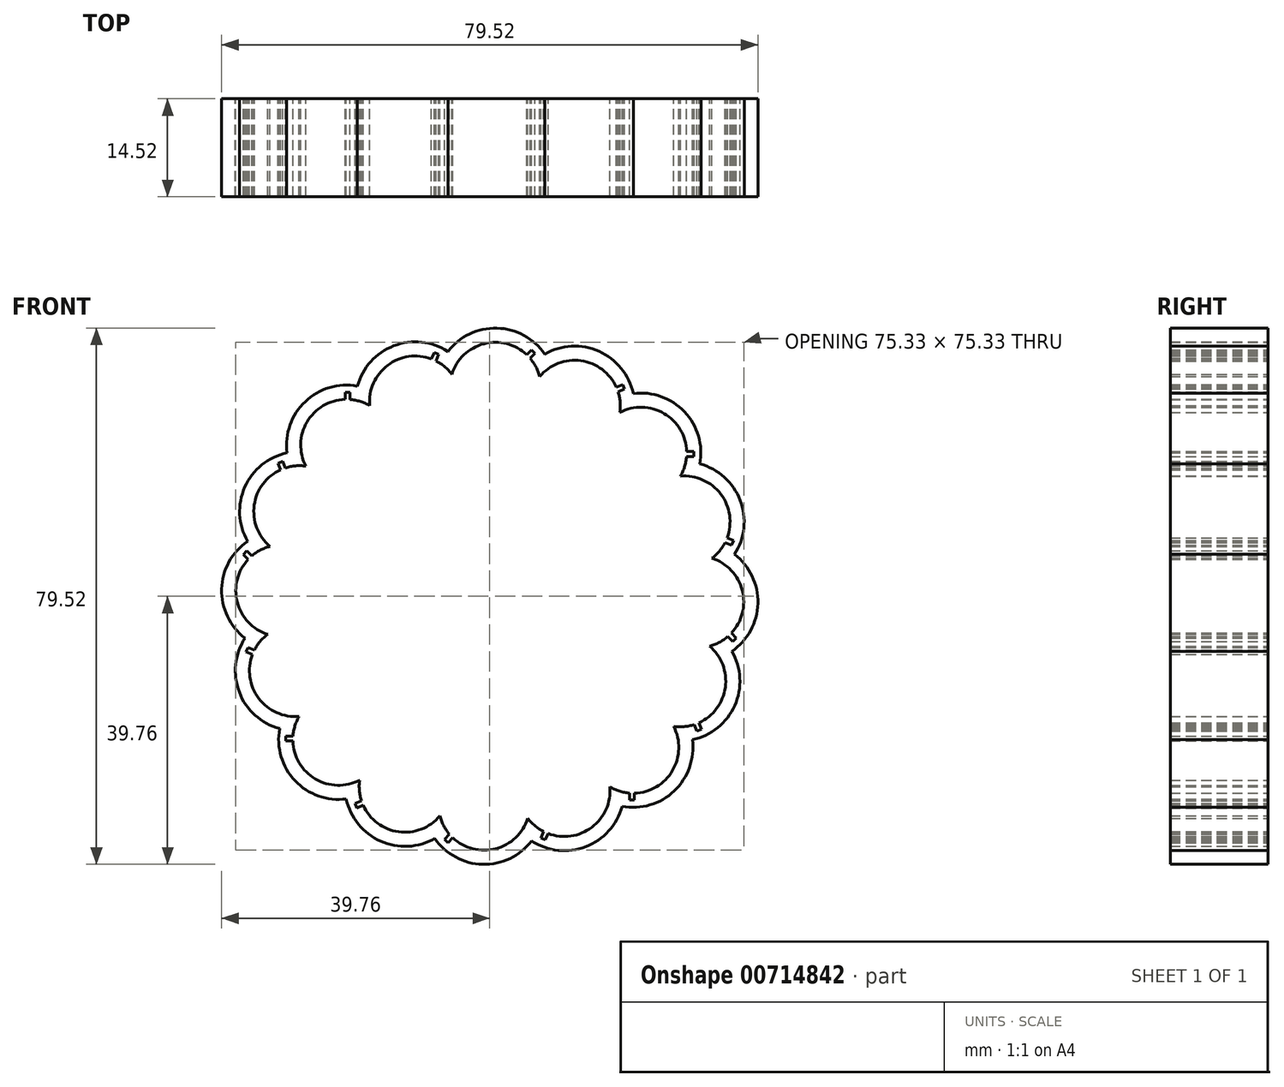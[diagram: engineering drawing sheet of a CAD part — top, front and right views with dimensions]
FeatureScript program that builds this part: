
annotation { "Feature Type Name" : "Feature", "Feature Type Description" : "" }
export const myFeature = defineFeature(function(context is Context, id is Id, definition is map)
    precondition{}
    {
        {
            var Q0;
            Q0=qCreatedBy(makeId("Front.planeOp"),FACE);
            var sketch = newSketch(context, id + "F0", { "sketchPlane" : qUnion([Q0])});
            skCircle(sketch, "E0", {"center": v(-21.25, 22.42) * mm, "radius": 6.79 * mm});
            skCircle(sketch, "E1", {"center": v(-21.25, 22.42) * mm, "radius": 4 * mm});
            skLineSegment(sketch, "E2.right", {"start": v(-21.46, 29.17) * mm, "end": v(-21.46, 29.2) * mm});
            skLineSegment(sketch, "E3.bottom", {"start": v(-21.46, 29.17) * mm, "end": v(-20.73, 29.17) * mm});
            skLineSegment(sketch, "E3.top", {"start": v(-21.46, 30.23) * mm, "end": v(-20.73, 30.23) * mm});
            skLineSegment(sketch, "E3.left", {"start": v(-21.46, 29.17) * mm, "end": v(-21.46, 30.23) * mm});
            skLineSegment(sketch, "E3.right", {"start": v(-20.73, 29.17) * mm, "end": v(-20.73, 30.23) * mm});
            skCircle(sketch, "E4", {"center": v(-21.25, 22.42) * mm, "radius": 8.89 * mm});
            skLineSegment(sketch, "E5.1.0", {"start": v(-30.31, 19.01) * mm, "end": v(-30.72, 20) * mm});
            skLineSegment(sketch, "E5.1.1", {"start": v(-30.99, 18.73) * mm, "end": v(-31.4, 19.72) * mm});
            skLineSegment(sketch, "E5.1.2", {"start": v(-31.4, 19.72) * mm, "end": v(-30.72, 20) * mm});
            skCircle(sketch, "E5.1.3", {"center": v(-28.21, 12.58) * mm, "radius": 8.89 * mm});
            skCircle(sketch, "E5.1.4", {"center": v(-28.21, 12.58) * mm, "radius": 6.79 * mm});
            skLineSegment(sketch, "E5.2.0", {"start": v(-35.28, 5.96) * mm, "end": v(-36.04, 6.72) * mm});
            skLineSegment(sketch, "E5.2.1", {"start": v(-35.8, 5.45) * mm, "end": v(-36.55, 6.2) * mm});
            skLineSegment(sketch, "E5.2.2", {"start": v(-36.55, 6.2) * mm, "end": v(-36.04, 6.72) * mm});
            skCircle(sketch, "E5.2.3", {"center": v(-30.88, 0.83) * mm, "radius": 8.89 * mm});
            skCircle(sketch, "E5.2.4", {"center": v(-30.88, 0.83) * mm, "radius": 6.79 * mm});
            skLineSegment(sketch, "E5.3.0", {"start": v(-34.88, -8) * mm, "end": v(-35.87, -7.58) * mm});
            skLineSegment(sketch, "E5.3.1", {"start": v(-35.16, -8.66) * mm, "end": v(-36.14, -8.25) * mm});
            skLineSegment(sketch, "E5.3.2", {"start": v(-36.14, -8.25) * mm, "end": v(-35.87, -7.58) * mm});
            skCircle(sketch, "E5.3.3", {"center": v(-28.85, -11.05) * mm, "radius": 8.89 * mm});
            skCircle(sketch, "E5.3.4", {"center": v(-28.85, -11.05) * mm, "radius": 6.79 * mm});
            skLineSegment(sketch, "E5.4.0", {"start": v(-29.17, -20.73) * mm, "end": v(-30.23, -20.73) * mm});
            skLineSegment(sketch, "E5.4.1", {"start": v(-29.17, -21.46) * mm, "end": v(-30.23, -21.46) * mm});
            skLineSegment(sketch, "E5.4.2", {"start": v(-30.23, -21.46) * mm, "end": v(-30.23, -20.73) * mm});
            skCircle(sketch, "E5.4.3", {"center": v(-22.42, -21.25) * mm, "radius": 8.89 * mm});
            skCircle(sketch, "E5.4.4", {"center": v(-22.42, -21.25) * mm, "radius": 6.79 * mm});
            skLineSegment(sketch, "E5.5.0", {"start": v(-19.01, -30.31) * mm, "end": v(-20, -30.72) * mm});
            skLineSegment(sketch, "E5.5.1", {"start": v(-18.73, -30.99) * mm, "end": v(-19.72, -31.4) * mm});
            skLineSegment(sketch, "E5.5.2", {"start": v(-19.72, -31.4) * mm, "end": v(-20, -30.72) * mm});
            skCircle(sketch, "E5.5.3", {"center": v(-12.58, -28.21) * mm, "radius": 8.89 * mm});
            skCircle(sketch, "E5.5.4", {"center": v(-12.58, -28.21) * mm, "radius": 6.79 * mm});
            skLineSegment(sketch, "E5.6.0", {"start": v(-5.96, -35.28) * mm, "end": v(-6.72, -36.04) * mm});
            skLineSegment(sketch, "E5.6.1", {"start": v(-5.45, -35.8) * mm, "end": v(-6.2, -36.55) * mm});
            skLineSegment(sketch, "E5.6.2", {"start": v(-6.2, -36.55) * mm, "end": v(-6.72, -36.04) * mm});
            skCircle(sketch, "E5.6.3", {"center": v(-0.83, -30.88) * mm, "radius": 8.89 * mm});
            skCircle(sketch, "E5.6.4", {"center": v(-0.83, -30.88) * mm, "radius": 6.79 * mm});
            skLineSegment(sketch, "E5.7.0", {"start": v(8, -34.88) * mm, "end": v(7.58, -35.87) * mm});
            skLineSegment(sketch, "E5.7.1", {"start": v(8.66, -35.16) * mm, "end": v(8.25, -36.14) * mm});
            skLineSegment(sketch, "E5.7.2", {"start": v(8.25, -36.14) * mm, "end": v(7.58, -35.87) * mm});
            skCircle(sketch, "E5.7.3", {"center": v(11.05, -28.85) * mm, "radius": 8.89 * mm});
            skCircle(sketch, "E5.7.4", {"center": v(11.05, -28.85) * mm, "radius": 6.79 * mm});
            skLineSegment(sketch, "E5.8.0", {"start": v(20.73, -29.17) * mm, "end": v(20.73, -30.23) * mm});
            skLineSegment(sketch, "E5.8.1", {"start": v(21.46, -29.17) * mm, "end": v(21.46, -30.23) * mm});
            skLineSegment(sketch, "E5.8.2", {"start": v(21.46, -30.23) * mm, "end": v(20.73, -30.23) * mm});
            skCircle(sketch, "E5.8.3", {"center": v(21.25, -22.42) * mm, "radius": 8.89 * mm});
            skCircle(sketch, "E5.8.4", {"center": v(21.25, -22.42) * mm, "radius": 6.79 * mm});
            skLineSegment(sketch, "E5.9.0", {"start": v(30.31, -19.01) * mm, "end": v(30.72, -20) * mm});
            skLineSegment(sketch, "E5.9.1", {"start": v(30.99, -18.73) * mm, "end": v(31.4, -19.72) * mm});
            skLineSegment(sketch, "E5.9.2", {"start": v(31.4, -19.72) * mm, "end": v(30.72, -20) * mm});
            skCircle(sketch, "E5.9.3", {"center": v(28.21, -12.58) * mm, "radius": 8.89 * mm});
            skCircle(sketch, "E5.9.4", {"center": v(28.21, -12.58) * mm, "radius": 6.79 * mm});
            skLineSegment(sketch, "E5.10.0", {"start": v(35.28, -5.96) * mm, "end": v(36.04, -6.72) * mm});
            skLineSegment(sketch, "E5.10.1", {"start": v(35.8, -5.45) * mm, "end": v(36.55, -6.2) * mm});
            skLineSegment(sketch, "E5.10.2", {"start": v(36.55, -6.2) * mm, "end": v(36.04, -6.72) * mm});
            skCircle(sketch, "E5.10.3", {"center": v(30.88, -0.83) * mm, "radius": 8.89 * mm});
            skCircle(sketch, "E5.10.4", {"center": v(30.88, -0.83) * mm, "radius": 6.79 * mm});
            skLineSegment(sketch, "E5.11.0", {"start": v(34.88, 8) * mm, "end": v(35.87, 7.58) * mm});
            skLineSegment(sketch, "E5.11.1", {"start": v(35.16, 8.66) * mm, "end": v(36.14, 8.25) * mm});
            skLineSegment(sketch, "E5.11.2", {"start": v(36.14, 8.25) * mm, "end": v(35.87, 7.58) * mm});
            skCircle(sketch, "E5.11.3", {"center": v(28.85, 11.05) * mm, "radius": 8.89 * mm});
            skCircle(sketch, "E5.11.4", {"center": v(28.85, 11.05) * mm, "radius": 6.79 * mm});
            skLineSegment(sketch, "E5.12.0", {"start": v(29.17, 20.73) * mm, "end": v(30.23, 20.73) * mm});
            skLineSegment(sketch, "E5.12.1", {"start": v(29.17, 21.46) * mm, "end": v(30.23, 21.46) * mm});
            skLineSegment(sketch, "E5.12.2", {"start": v(30.23, 21.46) * mm, "end": v(30.23, 20.73) * mm});
            skCircle(sketch, "E5.12.3", {"center": v(22.42, 21.25) * mm, "radius": 8.89 * mm});
            skCircle(sketch, "E5.12.4", {"center": v(22.42, 21.25) * mm, "radius": 6.79 * mm});
            skLineSegment(sketch, "E5.13.0", {"start": v(19.01, 30.31) * mm, "end": v(20, 30.72) * mm});
            skLineSegment(sketch, "E5.13.1", {"start": v(18.73, 30.99) * mm, "end": v(19.72, 31.4) * mm});
            skLineSegment(sketch, "E5.13.2", {"start": v(19.72, 31.4) * mm, "end": v(20, 30.72) * mm});
            skCircle(sketch, "E5.13.3", {"center": v(12.58, 28.21) * mm, "radius": 8.89 * mm});
            skCircle(sketch, "E5.13.4", {"center": v(12.58, 28.21) * mm, "radius": 6.79 * mm});
            skLineSegment(sketch, "E5.14.0", {"start": v(5.96, 35.28) * mm, "end": v(6.72, 36.04) * mm});
            skLineSegment(sketch, "E5.14.1", {"start": v(5.45, 35.8) * mm, "end": v(6.2, 36.55) * mm});
            skLineSegment(sketch, "E5.14.2", {"start": v(6.2, 36.55) * mm, "end": v(6.72, 36.04) * mm});
            skCircle(sketch, "E5.14.3", {"center": v(0.83, 30.88) * mm, "radius": 8.89 * mm});
            skCircle(sketch, "E5.14.4", {"center": v(0.83, 30.88) * mm, "radius": 6.79 * mm});
            skLineSegment(sketch, "E5.15.0", {"start": v(-8, 34.88) * mm, "end": v(-7.58, 35.87) * mm});
            skLineSegment(sketch, "E5.15.1", {"start": v(-8.66, 35.16) * mm, "end": v(-8.25, 36.14) * mm});
            skLineSegment(sketch, "E5.15.2", {"start": v(-8.25, 36.14) * mm, "end": v(-7.58, 35.87) * mm});
            skCircle(sketch, "E5.15.3", {"center": v(-11.05, 28.85) * mm, "radius": 8.89 * mm});
            skCircle(sketch, "E5.15.4", {"center": v(-11.05, 28.85) * mm, "radius": 6.79 * mm});
            skPoint(sketch, "E5.center", {"position": v(0, 0) * mm});
            skSolve(sketch);
        }
        {
            var Q0;
            Q0 = qSketchRegion(id + "F0", true);
            extrude(context, id + "F1", {"entities" : qUnion([Q0]), "depth" : 14.52 * mm, "offsetDistance" : 25 * mm});
        }
    });
